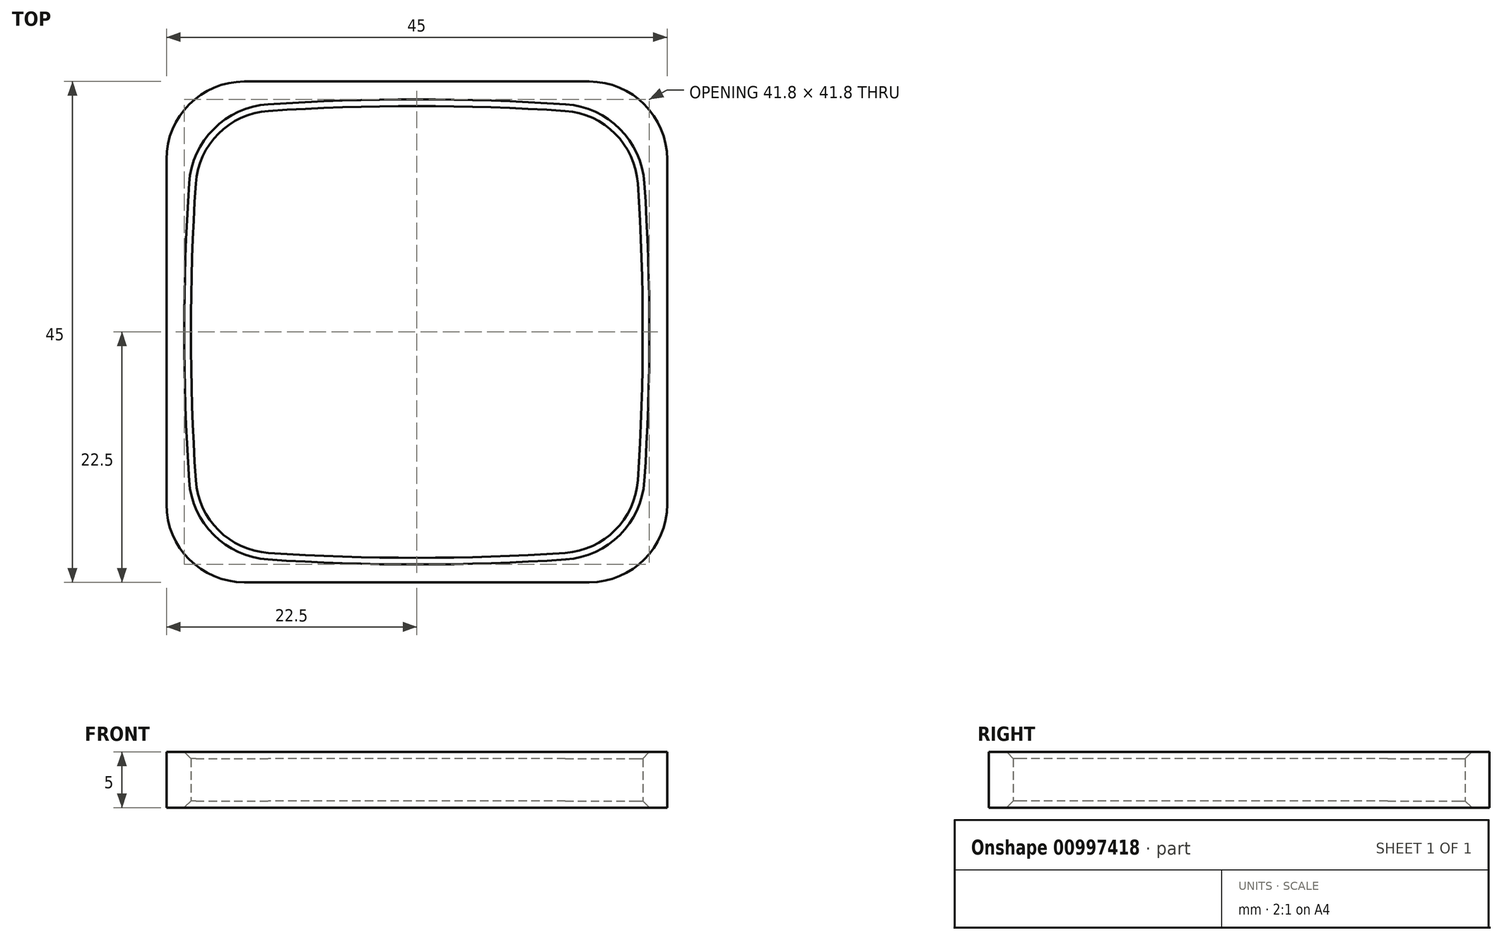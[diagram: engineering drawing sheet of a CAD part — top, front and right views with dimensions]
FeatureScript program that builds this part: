
annotation { "Feature Type Name" : "Feature", "Feature Type Description" : "" }
export const myFeature = defineFeature(function(context is Context, id is Id, definition is map)
    precondition{}
    {
        {
            var Q0;
            Q0=qCreatedBy(makeId("Top.planeOp"),FACE);
            var sketch = newSketch(context, id + "F0", { "sketchPlane" : qUnion([Q0])});
            skLineSegment(sketch, "E0.bottom", {"start": v(20.3, 20.3) * mm, "end": v(-20.3, 20.3) * mm, "construction": true});
            skLineSegment(sketch, "E0.top", {"start": v(20.3, -20.3) * mm, "end": v(-20.3, -20.3) * mm, "construction": true});
            skLineSegment(sketch, "E0.left", {"start": v(20.3, 20.3) * mm, "end": v(20.3, -20.3) * mm, "construction": true});
            skLineSegment(sketch, "E0.right", {"start": v(-20.3, 20.3) * mm, "end": v(-20.3, -20.3) * mm, "construction": true});
            skPoint(sketch, "E0.middle", {"position": v(0, 0) * mm});
            skArc(sketch, "E1", {"start": v(20.3, 19.27) * mm, "mid": v(0, 20.3) * mm, "end": v(-20.3, 19.27) * mm});
            skArc(sketch, "E2.1.0", {"start": v(-19.27, 20.3) * mm, "mid": v(-20.3, 0) * mm, "end": v(-19.27, -20.3) * mm});
            skArc(sketch, "E2.2.0", {"start": v(-20.3, -19.27) * mm, "mid": v(0, -20.3) * mm, "end": v(20.3, -19.27) * mm});
            skArc(sketch, "E2.3.0", {"start": v(19.27, -20.3) * mm, "mid": v(20.3, 0) * mm, "end": v(19.27, 20.3) * mm});
            skLineSegment(sketch, "E3.bottom", {"start": v(22.5, 22.5) * mm, "end": v(-22.5, 22.5) * mm});
            skLineSegment(sketch, "E3.top", {"start": v(22.5, -22.5) * mm, "end": v(-22.5, -22.5) * mm});
            skLineSegment(sketch, "E3.left", {"start": v(22.5, 22.5) * mm, "end": v(22.5, -22.5) * mm});
            skLineSegment(sketch, "E3.right", {"start": v(-22.5, 22.5) * mm, "end": v(-22.5, -22.5) * mm});
            skSolve(sketch);
        }
        {
            var Q0;
            Q0=makeQuery(id+"F0.imprint","IMPRINT",FACE,{"disambiguationData":[TD([[makeQuery(id+"F0.imprint","IMPRINT",EDGE,{"derivedFrom":sQuery(id+"F0.wireOp",EDGE,"E3.bottom")}),1.0]])]});
            extrude(context, id + "F1", {"entities" : qUnion([Q0]), "depth" : 5 * mm, "offsetDistance" : 25 * mm});
        }
        {
            var Q0;
            Q0=makeQuery(id+"F1.opExtrude","SWEPT_EDGE",EDGE,{"disambiguationData":[OSD([sQuery(id+"F0.wireOp",EDGE,"E1"),sQuery(id+"F0.wireOp",EDGE,"E2.1.0")])]});
            var Q1;
            Q1=makeQuery(id+"F1.opExtrude","SWEPT_EDGE",EDGE,{"disambiguationData":[OSD([sQuery(id+"F0.wireOp",EDGE,"E1"),sQuery(id+"F0.wireOp",EDGE,"E2.3.0")])]});
            var Q2;
            Q2=makeQuery(id+"F1.opExtrude","SWEPT_EDGE",EDGE,{"disambiguationData":[OSD([sQuery(id+"F0.wireOp",EDGE,"E2.2.0"),sQuery(id+"F0.wireOp",EDGE,"E2.3.0")])]});
            var Q3;
            Q3=makeQuery(id+"F1.opExtrude","SWEPT_EDGE",EDGE,{"disambiguationData":[OSD([sQuery(id+"F0.wireOp",EDGE,"E2.1.0"),sQuery(id+"F0.wireOp",EDGE,"E2.2.0")])]});
            var Q4;
            Q4=makeQuery(id+"F1.opExtrude","SWEPT_EDGE",EDGE,{"disambiguationData":[OSD([sQuery(id+"F0.wireOp",EDGE,"E3.bottom"),sQuery(id+"F0.wireOp",EDGE,"E3.right")])]});
            var Q5;
            Q5=makeQuery(id+"F1.opExtrude","SWEPT_EDGE",EDGE,{"disambiguationData":[OSD([sQuery(id+"F0.wireOp",EDGE,"E3.bottom"),sQuery(id+"F0.wireOp",EDGE,"E3.left")])]});
            var Q6;
            Q6=makeQuery(id+"F1.opExtrude","SWEPT_EDGE",EDGE,{"disambiguationData":[OSD([sQuery(id+"F0.wireOp",EDGE,"E3.top"),sQuery(id+"F0.wireOp",EDGE,"E3.left")])]});
            var Q7;
            Q7=makeQuery(id+"F1.opExtrude","SWEPT_EDGE",EDGE,{"disambiguationData":[OSD([sQuery(id+"F0.wireOp",EDGE,"E3.top"),sQuery(id+"F0.wireOp",EDGE,"E3.right")])]});
            fillet(context, id + "F2", {"entities" : qUnion([Q0, Q1, Q2, Q3, Q4, Q5, Q6, Q7]), "radius" : 7 * mm, "tangentPropagation" : true, "allowEdgeOverflow" : false});
        }
        {
            var Q0;
            Q0=makeQuery(id+"F1.opExtrude","CAP_EDGE",EDGE,{"disambiguationData":[OSD([sQuery(id+"F0.wireOp",EDGE,"E2.1.0")])],"isStart":false});
            var Q1;
            Q1=makeQuery(id+"F1.opExtrude","CAP_EDGE",EDGE,{"disambiguationData":[OSD([sQuery(id+"F0.wireOp",EDGE,"E2.1.0")])],"isStart":true});
            chamfer(context, id + "F3", {"entities" : qUnion([Q0, Q1]), "width" : 0.6 * mm, "tangentPropagation" : true});
        }
    });
